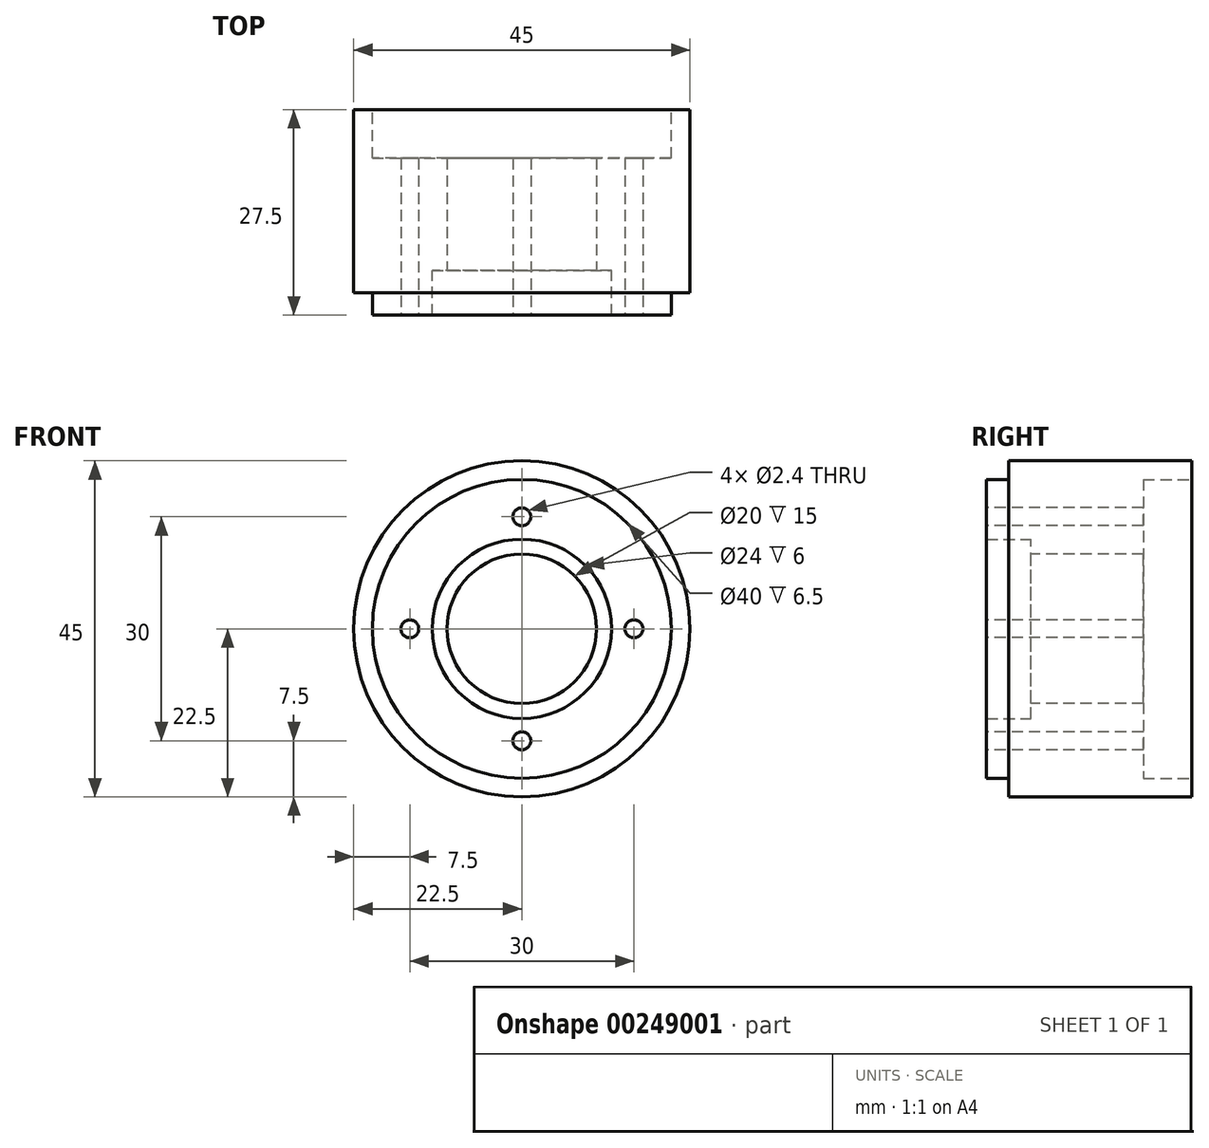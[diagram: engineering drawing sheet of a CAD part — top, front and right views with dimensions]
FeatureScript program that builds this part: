
annotation { "Feature Type Name" : "Feature", "Feature Type Description" : "" }
export const myFeature = defineFeature(function(context is Context, id is Id, definition is map)
    precondition{}
    {
        {
            var Q0;
            Q0=qCreatedBy(makeId("Front.planeOp"),FACE);
            var sketch = newSketch(context, id + "F12", { "sketchPlane" : qUnion([Q0])});
            skCircle(sketch, "E0", {"center": v(0, 0) * mm, "radius": 22.5 * mm});
            skSolve(sketch);
        }
        {
            var Q0;
            Q0=makeQuery(id+"F12.imprint","IMPRINT",FACE,{"disambiguationData":[TD([[makeQuery(id+"F12.imprint","IMPRINT",EDGE,{"derivedFrom":sQuery(id+"F12.wireOp",EDGE,"E0")}),1.0]])]});
            extrude(context, id + "F0", {"entities" : qUnion([Q0]), "endBound" : BoundingType.SYMMETRIC, "depth" : 29 * mm});
        }
        {
            var Q0;
            Q0=makeQuery(id+"F0.opExtrude","CAP_FACE",FACE,{"disambiguationData":[OSD([sQuery(id+"F12.wireOp",EDGE,"E0")])],"isStart":false});
            var sketch = newSketch(context, id + "F1", { "sketchPlane" : qUnion([Q0])});
            skPoint(sketch, "E1", {"position": v(0, 0) * mm});
            skCircle(sketch, "E2", {"center": v(0, 0) * mm, "radius": 12 * mm});
            skCircle(sketch, "E3", {"center": v(0, 0) * mm, "radius": 20 * mm});
            skPoint(sketch, "E4", {"position": v(15, 0) * mm});
            skPoint(sketch, "E5", {"position": v(0, -15) * mm});
            skPoint(sketch, "E6", {"position": v(-15, 0) * mm});
            skPoint(sketch, "E7", {"position": v(0, 15) * mm});
            skSolve(sketch);
        }
        {
            var Q0;
            Q0=sQuery(id+"F1.wireOp",VERTEX,"E1");
            var Q1;
            Q1=makeQuery(id+"F0.opExtrude","SWEPT_BODY",BODY,{"disambiguationData":[OSD([sQuery(id+"F12.wireOp",EDGE,"E0")])]});
            hole(context, id + "F2", {"style" : HoleStyle.SIMPLE, "endStyle" : HoleEndStyle.THROUGH, "holeDiameter" : 20 * mm, "tappedDepth" : 12 * mm, "tapClearance" : 3, "startFromSketch" : true, "locations" : qUnion([Q0]), "scope" : qUnion([Q1])});
        }
        {
            var Q0;
            Q0=makeQuery(id+"F1.imprint","IMPRINT",FACE,{"disambiguationData":[TD([[makeQuery(id+"F1.imprint","IMPRINT",EDGE,{"derivedFrom":sQuery(id+"F1.wireOp",EDGE,"E2")}),-1.0]])]});
            var Q1;
            Q1=sQuery(id+"F1.wireOp",EDGE,"E3");
            extrude(context, id + "F3", {"entities" : qUnion([Q0]), "operationType" : NewBodyOperationType.ADD, "surfaceEntities" : qUnion([Q1]), "depth" : 3 * mm});
        }
        {
            var Q0;
            Q0=makeQuery(id+"F1.imprint","IMPRINT",FACE,{"disambiguationData":[TD([[makeQuery(id+"F1.imprint","IMPRINT",EDGE,{"derivedFrom":sQuery(id+"F1.wireOp",EDGE,"E2")}),1.0]])]});
            extrude(context, id + "F4", {"entities" : qUnion([Q0]), "operationType" : NewBodyOperationType.REMOVE, "oppositeDirection" : true, "depth" : 3 * mm});
        }
        {
            var Q0;
            Q0=makeQuery(id+"F0.opExtrude","CAP_FACE",FACE,{"disambiguationData":[OSD([sQuery(id+"F12.wireOp",EDGE,"E0")])],"isStart":true});
            var sketch = newSketch(context, id + "F5", { "sketchPlane" : qUnion([Q0])});
            skCircle(sketch, "E8.0.0", {"center": v(0, 0) * mm, "radius": 22.5 * mm});
            skCircle(sketch, "E9.0", {"center": v(0, 0) * mm, "radius": 20 * mm});
            skCircle(sketch, "E10.0", {"center": v(0, 0) * mm, "radius": 12 * mm});
            skCircle(sketch, "E11.0", {"center": v(0, 0) * mm, "radius": 10 * mm});
            skPoint(sketch, "E12.0", {"position": v(15, 0) * mm});
            skPoint(sketch, "E13.0", {"position": v(0, 15) * mm});
            skPoint(sketch, "E14.0", {"position": v(-15, 0) * mm});
            skPoint(sketch, "E15.0", {"position": v(0, -15) * mm});
            skSolve(sketch);
        }
        {
            var Q0;
            Q0=makeQuery(id+"F5.imprint","IMPRINT",FACE,{"disambiguationData":[TD([[makeQuery(id+"F5.imprint","IMPRINT",EDGE,{"derivedFrom":sQuery(id+"F5.wireOp",EDGE,"E9.0")}),-1.0]])]});
            extrude(context, id + "F6", {"entities" : qUnion([Q0]), "operationType" : NewBodyOperationType.REMOVE, "oppositeDirection" : true, "depth" : 4.5 * mm});
        }
        {
            var Q0;
            Q0=makeQuery(id+"F6.boolean.opBoolean","SPLIT",FACE,{"disambiguationData":[TD([makeQuery(id+"F2.hole-0.boolean.opBoolean","COPY",FACE,{"derivedFrom":makeQuery(id+"F2.hole-0.opRevolve","SWEPT_FACE",FACE,{"disambiguationData":[OSD([sQuery(id+"F2.hole-0.sketch.wireOp",EDGE,"core_line_2")])]})})])],"derivedFrom":makeQuery(id+"F0.opExtrude","CAP_FACE",FACE,{"disambiguationData":[OSD([sQuery(id+"F12.wireOp",EDGE,"E0")])],"isStart":true})});
            extrude(context, id + "F7", {"entities" : qUnion([Q0]), "operationType" : NewBodyOperationType.REMOVE, "oppositeDirection" : true, "depth" : 11 * mm});
        }
        {
            var Q0;
            Q0=makeQuery(id+"F3.opExtrude","CAP_FACE",FACE,{"disambiguationData":[OSD([sQuery(id+"F1.wireOp",EDGE,"E2"),sQuery(id+"F1.wireOp",EDGE,"E3")])],"isStart":false});
            var sketch = newSketch(context, id + "F8", { "sketchPlane" : qUnion([Q0])});
            skPoint(sketch, "E16.0", {"position": v(0, 15) * mm});
            skPoint(sketch, "E17.0", {"position": v(15, 0) * mm});
            skPoint(sketch, "E18.0", {"position": v(0, -15) * mm});
            skPoint(sketch, "E19.0", {"position": v(-15, 0) * mm});
            skSolve(sketch);
        }
        {
            var Q0;
            Q0=sQuery(id+"F8.wireOp",VERTEX,"E19.0");
            var Q1;
            Q1=sQuery(id+"F8.wireOp",VERTEX,"E16.0");
            var Q2;
            Q2=sQuery(id+"F8.wireOp",VERTEX,"E17.0");
            var Q3;
            Q3=sQuery(id+"F8.wireOp",VERTEX,"E18.0");
            var Q4;
            Q4=makeQuery(id+"F0.opExtrude","SWEPT_BODY",BODY,{"disambiguationData":[OSD([sQuery(id+"F12.wireOp",EDGE,"E0")])]});
            hole(context, id + "F9", {"style" : HoleStyle.SIMPLE, "endStyle" : HoleEndStyle.BLIND, "standardTappedOrClearance" : lookupTablePath({ "standard" : "ISO", "engagement" : "75%", "pitch" : "0.6 mm", "size" : "M3", "type" : "Tapped" }), "standardBlindInLast" : lookupTablePath({ "standard" : "ISO", "engagement" : "75%", "pitch" : "0.6 mm", "size" : "M3", "type" : "Tapped" }), "holeDiameter" : 2.4 * mm, "showTappedDepth" : true, "holeDepth" : 13.8 * mm, "tappedDepth" : 12 * mm, "tapClearance" : 3, "startFromSketch" : true, "locations" : qUnion([Q0, Q1, Q2, Q3]), "scope" : qUnion([Q4])});
        }
        {
            var Q0;
            Q0=makeQuery(id+"F6.boolean.opBoolean","COPY",FACE,{"derivedFrom":makeQuery(id+"F6.opExtrude","CAP_FACE",FACE,{"disambiguationData":[OSD([sQuery(id+"F5.wireOp",EDGE,"E9.0"),sQuery(id+"F5.wireOp",EDGE,"E10.0")])],"isStart":false})});
            var sketch = newSketch(context, id + "F10", { "sketchPlane" : qUnion([Q0])});
            skPoint(sketch, "E20.0", {"position": v(-15, 0) * mm});
            skPoint(sketch, "E21.0", {"position": v(0, 15) * mm});
            skPoint(sketch, "E22.0", {"position": v(15, 0) * mm});
            skPoint(sketch, "E23.0", {"position": v(0, -15) * mm});
            skSolve(sketch);
        }
        {
            var Q0;
            Q0=sQuery(id+"F10.wireOp",VERTEX,"E20.0");
            var Q1;
            Q1=sQuery(id+"F10.wireOp",VERTEX,"E21.0");
            var Q2;
            Q2=sQuery(id+"F10.wireOp",VERTEX,"E22.0");
            var Q3;
            Q3=sQuery(id+"F10.wireOp",VERTEX,"E23.0");
            var Q4;
            Q4=makeQuery(id+"F0.opExtrude","SWEPT_BODY",BODY,{"disambiguationData":[OSD([sQuery(id+"F12.wireOp",EDGE,"E0")])]});
            hole(context, id + "F11", {"style" : HoleStyle.SIMPLE, "endStyle" : HoleEndStyle.BLIND, "standardTappedOrClearance" : lookupTablePath({ "standard" : "ISO", "engagement" : "75%", "pitch" : "0.6 mm", "size" : "M3", "type" : "Tapped" }), "standardBlindInLast" : lookupTablePath({ "standard" : "ISO", "engagement" : "75%", "pitch" : "0.6 mm", "size" : "M3", "type" : "Tapped" }), "holeDiameter" : 2.4 * mm, "showTappedDepth" : true, "holeDepth" : 13.8 * mm, "tappedDepth" : 12 * mm, "tapClearance" : 3, "startFromSketch" : true, "locations" : qUnion([Q0, Q1, Q2, Q3]), "scope" : qUnion([Q4])});
        }
    });
